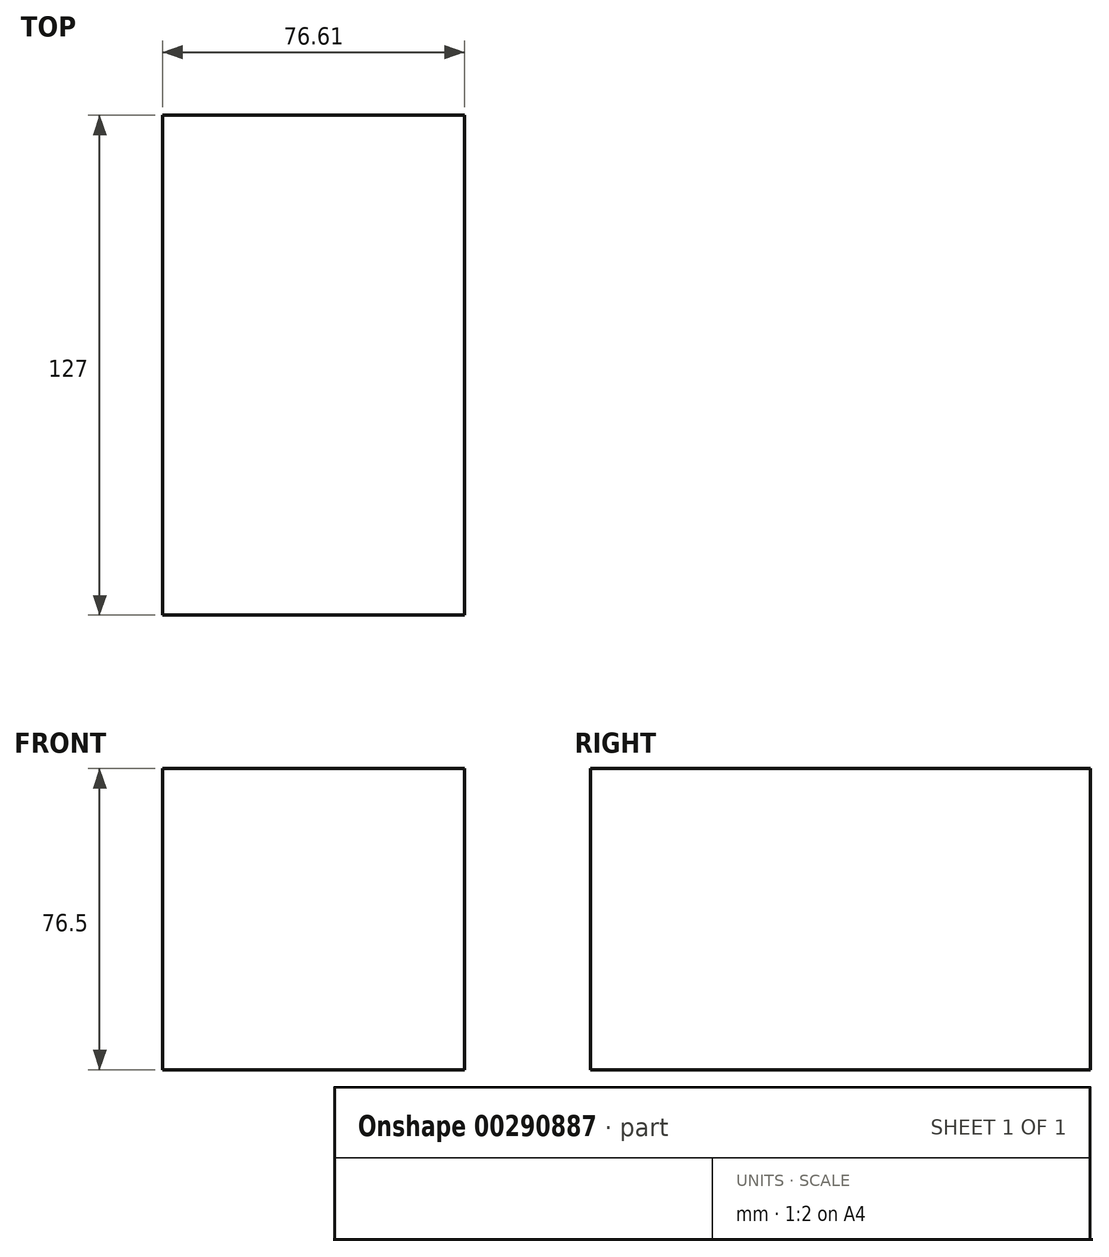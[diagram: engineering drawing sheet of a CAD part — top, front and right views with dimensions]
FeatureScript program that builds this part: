
annotation { "Feature Type Name" : "Feature", "Feature Type Description" : "" }
export const myFeature = defineFeature(function(context is Context, id is Id, definition is map)
    precondition{}
    {
        {
            var Q0;
            Q0=qCreatedBy(makeId("Front.planeOp"),FACE);
            var sketch = newSketch(context, id + "F0", { "sketchPlane" : qUnion([Q0])});
            skLineSegment(sketch, "E0.bottom", {"start": v(0, 0) * mm, "end": v(76.61, 0) * mm});
            skLineSegment(sketch, "E0.top", {"start": v(0, 76.5) * mm, "end": v(76.61, 76.5) * mm});
            skLineSegment(sketch, "E0.left", {"start": v(0, 0) * mm, "end": v(0, 76.5) * mm});
            skLineSegment(sketch, "E0.right", {"start": v(76.61, 0) * mm, "end": v(76.61, 76.5) * mm});
            skSolve(sketch);
        }
        {
            var Q0;
            Q0 = qSketchRegion(id + "F0", true);
            extrude(context, id + "F1", {"entities" : qUnion([Q0]), "depth" : 127 * mm});
        }
    });
